# Revit family: Building-IEC309Connections-GEWISS-IEC309HP-10°_FLUSH-MOUNT_SOCKET_FAST_WIRING_32A_IP44-54
name_source: partatom
category: Apparecchi elettrici
units: mm (PartAtom-declared; Revit-internal decimal feet)

## family parameters
Condiviso = No
Host = Superficie
Mantenere orientamento annotazione = Sì
Punto di calcolo locali = Sì
Quota connettore circolare = Usa diametro
Taglio con vuoti quando caricato = No
Tipo di parte = Normale

## types (9) — shared parameters
BLOCCO = B=C
Breaking capacity at 1.1 Un = 40A
Catalogue = BUILDING
Corpo centrale = Default(2)
Electrocod = 2210
FORMULA = 1000 mm  [stored 3.28084 ft]
Flange dimensions (mm) = 95x80
Frequency = 50/60 Hz
Glow wire test: = 850 °C (active parts) - 650 °C (passive parts)
IDF = 07cd4bf5-9810-4cbd-96a6-5ef965e97edd
IDT = ea62251e904f421b863a0432afd0cde4
IP degree = IP44/IP54
Immagine tipo = <Nessuno>
Insulation resistance = - 10 M?
L = 155 mm
N.poli = 1
Operating temperature: = -25 +55 °C
Permissible overload = 42A
Piastra = Default(2)
Produttore = GEWISS S.p.A.
Prospetto di default = 1219 mm
Rated current (A) = 32
SEO = Socket outlet
SPinotto = Default(2)
Shock resistance = IK09
Sportello_visibile = Sì
Spostamento_S = 963 mm
Technical sheet = https://www.gewiss.com
Terminal tightening capacity = 2.5-6mm² flexible cables - 2.5-10mm² rigid cables
Thermo-pressure with ball = 125 °C (active parts) - 80 °C (passive parts)
Total number of operations = -2000
Type of material = Halogen-free in compliance with EN 60754-2
Type of wiring = Quick, with spring
Typology = 10° angled flush-mounting socket-outlet
URL = https://www.gewiss.com
Version file RFA = 21.11
Voltaggio = 0 V
W = 115 mm

## per-type parameters (varying)
| type | Colour: | Descrizione | Modello | No. of poles | Rated voltage | Reference h |
| GW62214FH - 10°FLUSH.S.O. HP IP44 3P+E 32A 110V4H FW | Yellow | 10°FLUSH.S.O. HP IP44 3P+E 32A 110V4H FW | GW62214FH | 3P+E | 100-130V | 4 |
| GW62218FH - 10°FL.S.O. HP IP44 3P+N+E 32A 230V 9H FW | Blue | 10°FL.S.O. HP IP44 3P+N+E 32A 230V 9H FW | GW62218FH | 3P+N+E | 200-250V | 9 |
| GW62213FH - 10°FLUSH.S.O. HP IP44 2P+E 32A 110V4H FW | Yellow | 10°FLUSH.S.O. HP IP44 2P+E 32A 110V4H FW | GW62213FH | 2P+E | 100-130V | 4 |
| GW62217FH - 10°FLUSH.S.O. HP IP44 3P+E 32A 230V9H FW | Blue | 10°FLUSH.S.O. HP IP44 3P+E 32A 230V9H FW | GW62217FH | 3P+E | 200-250V | 9 |
| GW62220FH - 10°FLUSH.S.O.HP IP44 3P+E 32A 400V 6H FW | Red | 10°FLUSH.S.O.HP IP44 3P+E 32A 400V 6H FW | GW62220FH | 3P+E | 380-415V | 6 |
| GW62215FH - 10°FL.S.O. HP IP44 3P+N+E 32A 110V 4H FW | Yellow | 10°FL.S.O. HP IP44 3P+N+E 32A 110V 4H FW | GW62215FH | 3P+N+E | 100-130V | 4 |
| GW62221FH - 10°FL.S.O.HP IP44 3P+N+E 32A 400V 6H FW | Red | 10°FL.S.O.HP IP44 3P+N+E 32A 400V 6H FW | GW62221FH | 3P+N+E | 380-415V | 6 |
| GW62216FH - 10°FLUSH.S.O. HP IP44 2P+E 32A 230V6H FW | Blue | 10°FLUSH.S.O. HP IP44 2P+E 32A 230V6H FW | GW62216FH | 2P+E | 200-250V | 6 |
| GW62219FH - 10°FLUSH.S.O.HP IP44 2P+E 32A 400V 9H FW | Red | 10°FLUSH.S.O.HP IP44 2P+E 32A 400V 9H FW | GW62219FH | 2P+E | 380-415V | 9 |

note: [stored X ft] marks values corroborated as IEEE doubles in the binary element streams (Revit-internal decimal feet)

## geometry (parser evidence)
native form markers: Sweep x1
no freeform markers — native parametric forms only
